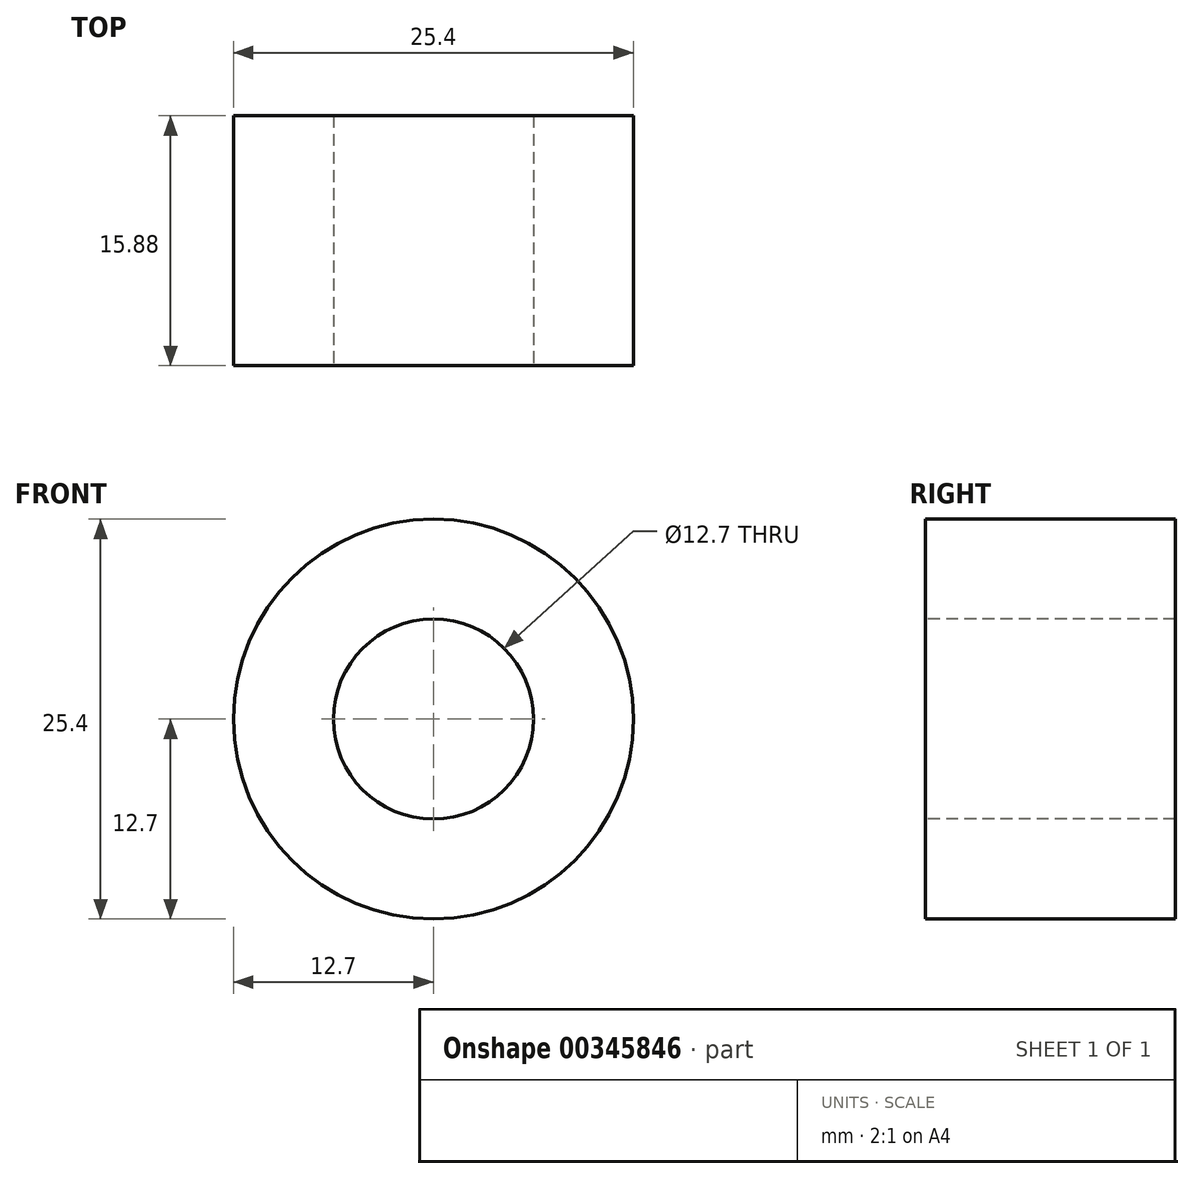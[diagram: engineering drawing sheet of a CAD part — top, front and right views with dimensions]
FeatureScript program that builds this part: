
annotation { "Feature Type Name" : "Feature", "Feature Type Description" : "" }
export const myFeature = defineFeature(function(context is Context, id is Id, definition is map)
    precondition{}
    {
        {
            var Q0;
            Q0=qCreatedBy(makeId("Front.planeOp"),FACE);
            var sketch = newSketch(context, id + "F1", { "sketchPlane" : qUnion([Q0])});
            skCircle(sketch, "E0", {"center": v(0, 0) * mm, "radius": 12.7 * mm});
            skCircle(sketch, "E1", {"center": v(0, 0) * mm, "radius": 6.35 * mm});
            skSolve(sketch);
        }
        {
            var Q0;
            Q0=makeQuery(id+"F1.imprint","IMPRINT",FACE,{"disambiguationData":[TD([[makeQuery(id+"F1.imprint","IMPRINT",EDGE,{"derivedFrom":sQuery(id+"F1.wireOp",EDGE,"E0")}),1.0]])]});
            extrude(context, id + "F0", {"entities" : qUnion([Q0]), "oppositeDirection" : true, "depth" : 15.88 * mm});
        }
    });
